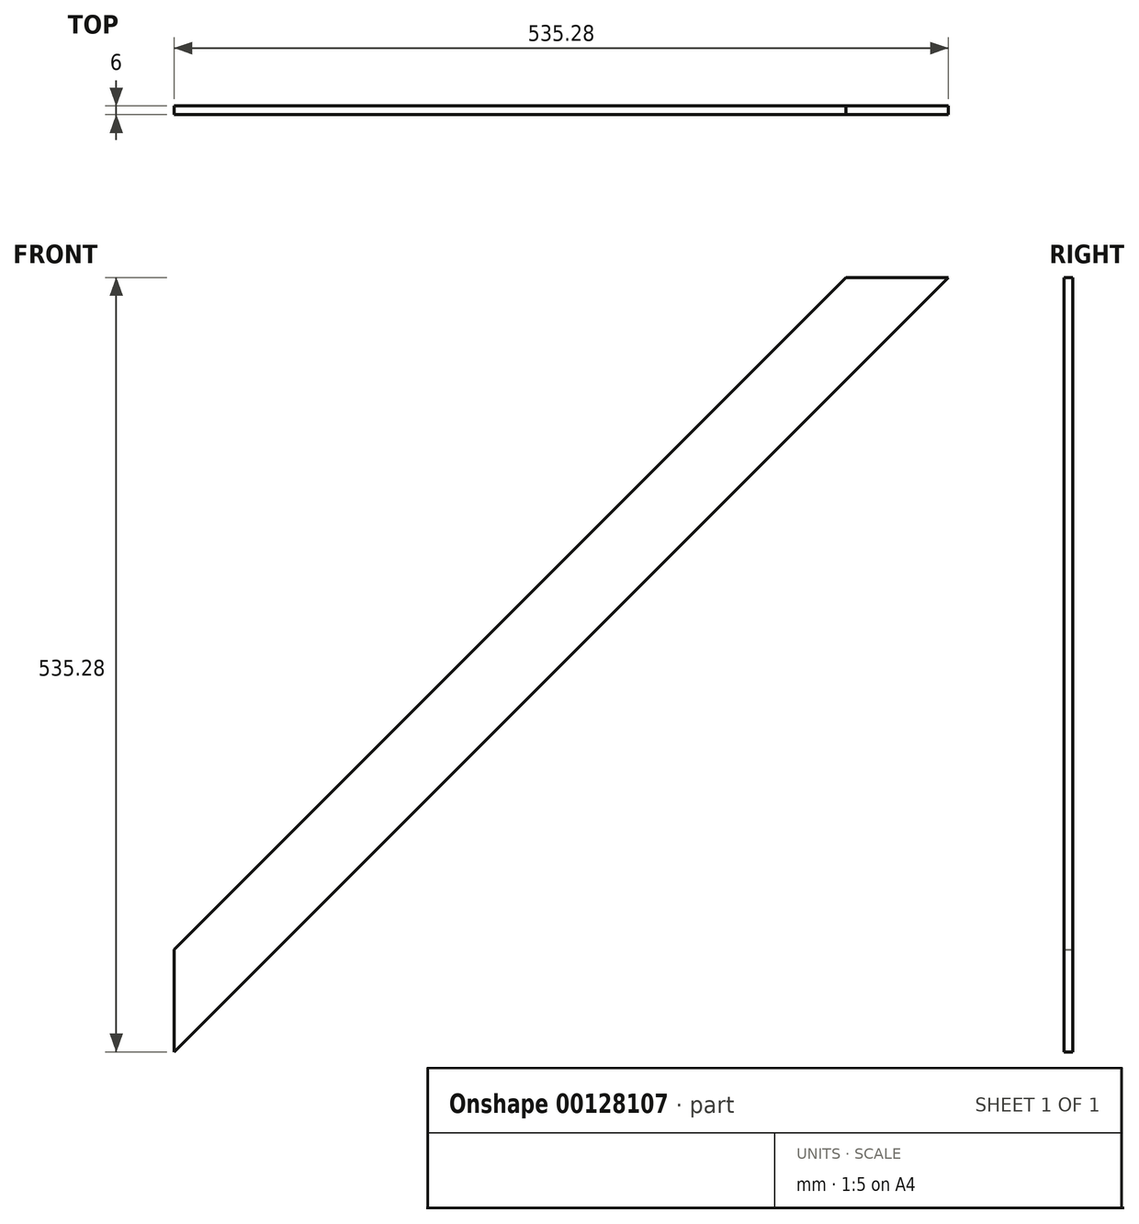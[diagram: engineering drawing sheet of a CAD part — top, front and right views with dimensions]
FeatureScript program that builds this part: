
annotation { "Feature Type Name" : "Feature", "Feature Type Description" : "" }
export const myFeature = defineFeature(function(context is Context, id is Id, definition is map)
    precondition{}
    {
        {
            var Q0;
            Q0=qCreatedBy(makeId("Front.planeOp"),FACE);
            var sketch = newSketch(context, id + "F0", { "sketchPlane" : qUnion([Q0])});
            skLineSegment(sketch, "E0", {"start": v(464.57, 499.92) * mm, "end": v(0, 35.36) * mm});
            skLineSegment(sketch, "E1", {"start": v(17.68, -17.68) * mm, "end": v(517.6, 482.25) * mm});
            skLineSegment(sketch, "E2", {"start": v(464.57, 499.92) * mm, "end": v(535.28, 499.92) * mm});
            skLineSegment(sketch, "E3", {"start": v(0, 35.36) * mm, "end": v(0, -35.36) * mm});
            skLineSegment(sketch, "E4", {"start": v(517.6, 482.25) * mm, "end": v(535.28, 499.92) * mm});
            skLineSegment(sketch, "E5", {"start": v(17.68, -17.68) * mm, "end": v(0, -35.36) * mm});
            skPoint(sketch, "E6.start.orphan", {"position": v(0, 0) * mm});
            skPoint(sketch, "E7.start.orphan", {"position": v(499.92, 499.92) * mm});
            skSolve(sketch);
        }
        {
            var Q0;
            Q0 = qSketchRegion(id + "F0", true);
            extrude(context, id + "F1", {"entities" : qUnion([Q0]), "depth" : 6 * mm});
        }
    });
